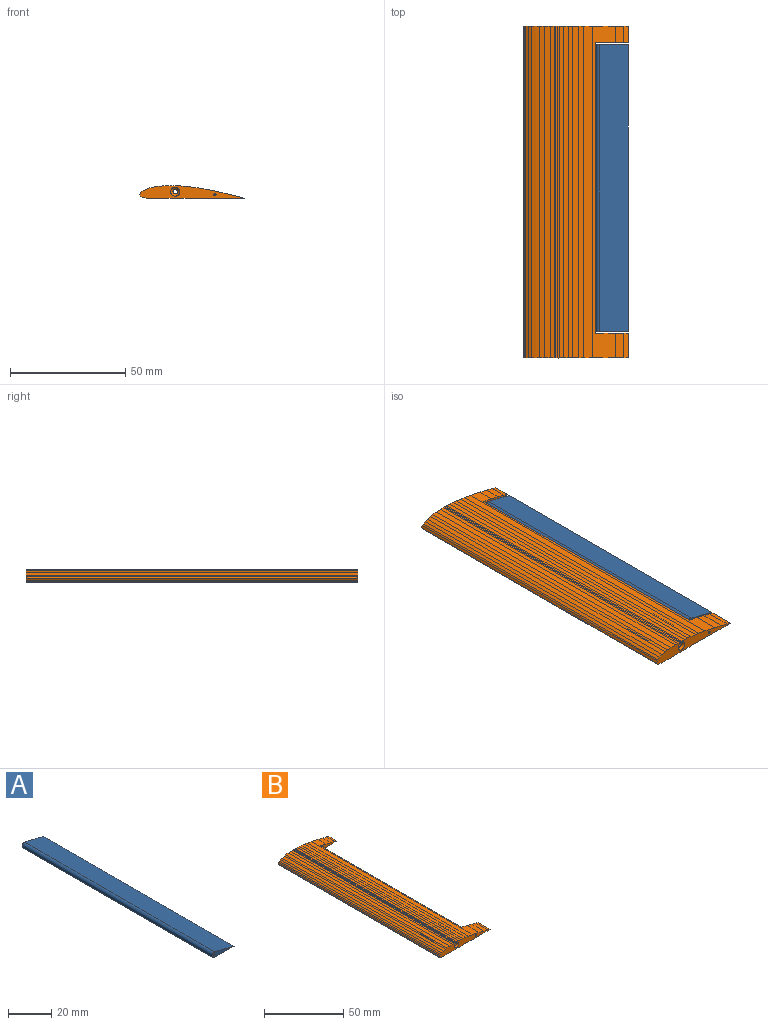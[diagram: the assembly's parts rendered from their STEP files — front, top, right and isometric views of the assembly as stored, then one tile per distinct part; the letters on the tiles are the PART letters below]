
ASSEMBLY  parts=2 mates=1
PART A: 6 faces, bbox 14.2x124.1x3.1 mm
  f0: plane 124.08x12.44mm, normal (0.24,0,0.97), area 1589.1mm2, adj f1,f2,f4,f5
  f1: cylinder r=1.46mm len=124.08mm, axis (0,1,0), area 609.3mm2, adj f0,f2,f4,f5
  f2: plane 124.08x12.81mm, normal (-0.01,0,-1), area 1589.1mm2, adj f0,f1,f4,f5
  f3: cylinder r=0.41mm len=124.08mm, axis (0,1,0), area 316mm2, adj f4,f5
  f4: plane 14.24x3.09mm, normal (0,-1,0), area 21.7mm2, adj f0,f1,f2,f3
  f5: plane 14.24x3.09mm, normal (0,1,0), area 21.7mm2, adj f0,f1,f2,f3
PART B: 67 faces, bbox 45.5x144x5.6 mm
  f0: plane 144x15.97mm, normal (0,0,-1), area 1535mm2, adj f6,f8,f28,f29,f55,f56,f59,f60
  f1: plane 144x1.77mm, normal (-0.01,0,-1), area 251mm2, adj f2,f23,f24,f55,f56,f62,f63,f65
  f2: plane 10.89x6.63mm, normal (0,0,-1), area 72.2mm2, adj f1,f3,f55,f63
  f3: plane 10.89x1.77mm, normal (0,0,-1), area 19.3mm2, adj f2,f4,f55,f63
  f4: plane 10.89x2.95mm, normal (0.01,0,-1), area 32.2mm2, adj f3,f5,f55,f63
  f5: plane 10.89x1.34mm, normal (0.02,0,-1), area 14.6mm2, adj f4,f6,f55,f63
  f6: plane 10.89x1.78mm, normal (0.02,0,-1), area 19.4mm2, adj f0,f5,f55,f63
  f7: cylinder r=0.97mm len=9.89mm, axis (0,1,0), area 60.1mm2, adj f57,f63
  f8: plane 10.7x2.09mm, normal (-0.02,0,-1), area 22.3mm2, adj f0,f9,f55,f59
  f9: plane 10.7x1.67mm, normal (-0.02,0,-1), area 17.8mm2, adj f8,f10,f55,f59
  f10: plane 10.7x2.11mm, normal (0,0,-1), area 22.5mm2, adj f9,f11,f55,f59
  f11: plane 10.7x2.61mm, normal (0.01,0,-1), area 27.9mm2, adj f10,f12,f55,f59
  f12: plane 10.7x2.05mm, normal (0.28,0,0.96), area 22.8mm2, adj f11,f13,f55,f59
  f13: plane 10.7x3.54mm, normal (0.25,0,0.97), area 39.1mm2, adj f12,f14,f55,f59
  f14: plane 10.7x4.19mm, normal (0.24,0,0.97), area 46.1mm2, adj f13,f15,f55,f59
  f15: plane 144x5.9mm, normal (0.21,0,0.98), area 267.7mm2, adj f14,f35,f36,f55,f56,f59,f60,f61
  f16: cylinder r=0.47mm len=10.7mm, axis (0,1,0), area 31.4mm2, adj f55,f59
  f17: plane 144x0.93mm, normal (-0.87,0,0.49), area 152.4mm2, adj f18,f53,f55,f56
  f18: plane 144x0.83mm, normal (-0.83,0,-0.56), area 143.7mm2, adj f17,f19,f55,f56
  f19: plane 144x0.52mm, normal (-0.4,0,-0.92), area 81.9mm2, adj f18,f20,f55,f56
  f20: plane 144x0.63mm, normal (-0.2,0,-0.98), area 92.9mm2, adj f19,f21,f55,f56
  f21: plane 144x1.2mm, normal (-0.14,0,-0.99), area 174mm2, adj f20,f22,f55,f56
  f22: plane 144x0.97mm, normal (-0.1,0,-1), area 140.2mm2, adj f21,f23,f55,f56
  f23: plane 144x0.93mm, normal (-0.06,0,-1), area 133.5mm2, adj f1,f22,f55,f56
  f24: plane 120.12x6.63mm, normal (0,0,-1), area 796mm2, adj f1,f25,f56,f65
  f25: plane 120.12x1.77mm, normal (0,0,-1), area 212.9mm2, adj f24,f26,f56,f65
  f26: plane 120.12x2.95mm, normal (0.01,0,-1), area 354.5mm2, adj f25,f27,f56,f65
  f27: plane 120.12x1.34mm, normal (0.02,0,-1), area 160.5mm2, adj f26,f28,f56,f65
  f28: plane 120.12x1.78mm, normal (0.02,0,-1), area 213.5mm2, adj f0,f27,f56,f65
  f29: plane 7.14x2.09mm, normal (-0.02,0,-1), area 14.9mm2, adj f0,f30,f56,f61
  f30: plane 7.14x1.67mm, normal (-0.02,0,-1), area 11.9mm2, adj f29,f31,f56,f61
  f31: plane 7.14x2.11mm, normal (0,0,-1), area 15mm2, adj f30,f32,f56,f61
  f32: plane 7.14x2.61mm, normal (0.01,0,-1), area 18.6mm2, adj f31,f33,f56,f61
  f33: plane 7.14x2.05mm, normal (0.28,0,0.96), area 15.2mm2, adj f32,f34,f56,f61
  f34: plane 7.14x3.54mm, normal (0.25,0,0.97), area 26.1mm2, adj f33,f35,f56,f61
  f35: plane 7.14x4.19mm, normal (0.24,0,0.97), area 30.7mm2, adj f15,f34,f56,f61
  f36: plane 144x3.73mm, normal (0.17,0,0.99), area 545.1mm2, adj f15,f37,f55,f56
  f37: plane 144x2.14mm, normal (0.15,0,0.99), area 312.5mm2, adj f36,f38,f55,f56
  f38: plane 144x2.66mm, normal (0.12,0,0.99), area 385.3mm2, adj f37,f39,f55,f56
  f39: plane 144x1.91mm, normal (0.09,0,1), area 276.1mm2, adj f38,f40,f55,f56
  f40: plane 144x2.04mm, normal (0.08,0,1), area 294.8mm2, adj f39,f41,f55,f56
  f41: plane 144x1.9mm, normal (0.06,0,1), area 274.3mm2, adj f40,f42,f55,f56
  f42: plane 144x0.77mm, normal (0,0,1), area 111mm2, adj f41,f43,f55,f56
  f43: plane 144x0.7mm, normal (0.04,0,1), area 100.7mm2, adj f42,f44,f55,f56
  f44: plane 144x0.75mm, normal (0,0,1), area 107.6mm2, adj f43,f45,f55,f56
  f45: plane 144x1.66mm, normal (-0.05,0,1), area 238.7mm2, adj f44,f46,f55,f56
  f46: plane 144x2.54mm, normal (-0.05,0,1), area 366.3mm2, adj f45,f47,f55,f56
  f47: plane 144x2.07mm, normal (-0.13,0,0.99), area 300.6mm2, adj f46,f48,f55,f56
  f48: plane 144x1.47mm, normal (-0.21,0,0.98), area 216.1mm2, adj f47,f49,f55,f56
  f49: plane 144x1.91mm, normal (-0.27,0,0.96), area 285.2mm2, adj f48,f50,f55,f56
  f50: plane 144x1.37mm, normal (-0.42,0,0.91), area 216.7mm2, adj f49,f51,f55,f56
  f51: plane 144x1.16mm, normal (-0.51,0,0.86), area 194.4mm2, adj f50,f53,f55,f56
  f52: cylinder r=0.97mm len=119.12mm, axis (0,1,0), area 723.8mm2, adj f58,f65
  f53: plane 144x0.51mm, normal (-0.69,0,0.73), area 101.7mm2, adj f17,f51,f55,f56
  f54: cylinder r=0.47mm len=7.14mm, axis (0,1,0), area 20.9mm2, adj f56,f61
  f55: plane 45.48x5.58mm, normal (0,-1,0), area 158.9mm2, adj f0,f1,f2,f3,f4,f5,f6,f8
  f56: plane 45.48x5.58mm, normal (0,1,0), area 158.9mm2, adj f0,f1,f15,f17,f18,f19,f20,f21
  f57: cone r=0.97mm half-angle=45deg, axis (0,-1,0), area 13mm2, adj f7,f55
  f58: cone r=1.97mm half-angle=45deg, axis (0,1,0), area 13mm2, adj f52,f56
  f59: plane 14.44x3.54mm, normal (0,1,0), area 25.9mm2, adj f0,f8,f9,f10,f11,f12,f13,f14
  f60: plane 126.17x3.46mm, normal (1,0,0), area 436.6mm2, adj f0,f15,f59,f61
  f61: plane 14.44x3.54mm, normal (0,-1,0), area 25.9mm2, adj f0,f15,f29,f30,f31,f32,f33,f34
  f62: plane 12.99x4.79mm, normal (1,0,0), area 62.2mm2, adj f1,f63,f65,f66
  f63: plane 15.69x4.8mm, normal (0,1,0), area 72mm2, adj f0,f1,f2,f3,f4,f5,f6,f7
  f64: plane 12.99x4.71mm, normal (-1,0,0), area 61.2mm2, adj f0,f63,f65,f66
  f65: plane 15.69x4.8mm, normal (0,-1,0), area 72mm2, adj f0,f1,f24,f25,f26,f27,f28,f52
  f66: plane 15.69x12.99mm, normal (0,0,-1), area 203.8mm2, adj f62,f63,f64,f65
PLACE A rot(axis=(0.92,0.09,0.38),0deg) t=(17.24,-16.25,-12.6)mm
PLACE B t=(17.17,-16.98,-12.64)mm
MATE revolute A.f1 <-> B.f16  axis (0,-1,0) through (27.89,-78.29,-10.97)mm
